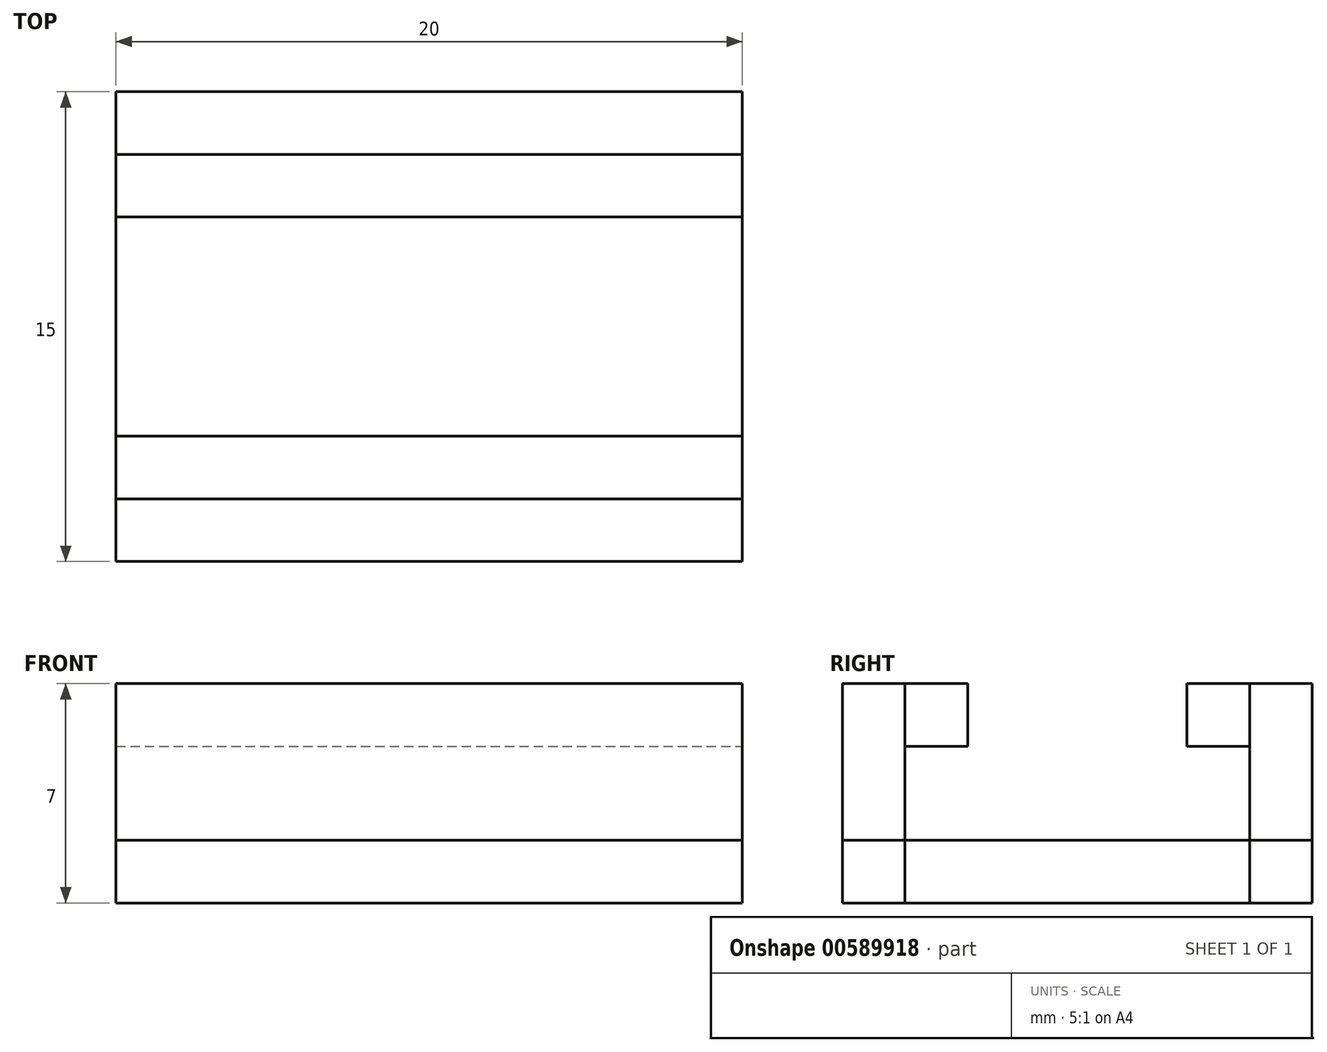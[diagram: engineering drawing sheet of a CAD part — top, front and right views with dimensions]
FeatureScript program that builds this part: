
annotation { "Feature Type Name" : "Feature", "Feature Type Description" : "" }
export const myFeature = defineFeature(function(context is Context, id is Id, definition is map)
    precondition{}
    {
        {
            var Q0;
            Q0=qCreatedBy(makeId("Top.planeOp"),FACE);
            var sketch = newSketch(context, id + "F0", { "sketchPlane" : qUnion([Q0])});
            skLineSegment(sketch, "E0.bottom", {"start": v(-43, 7.5) * mm, "end": v(-23, 7.5) * mm});
            skLineSegment(sketch, "E0.top", {"start": v(-43, -7.5) * mm, "end": v(-23, -7.5) * mm});
            skLineSegment(sketch, "E0.left", {"start": v(-43, 7.5) * mm, "end": v(-43, -7.5) * mm});
            skLineSegment(sketch, "E0.right", {"start": v(-23, 7.5) * mm, "end": v(-23, -7.5) * mm});
            skLineSegment(sketch, "E1.top", {"start": v(-43, 5.5) * mm, "end": v(-23, 5.5) * mm});
            skLineSegment(sketch, "E1.left", {"start": v(-43, 7.5) * mm, "end": v(-43, 5.5) * mm});
            skLineSegment(sketch, "E1.right", {"start": v(-23, 7.5) * mm, "end": v(-23, 5.5) * mm});
            skLineSegment(sketch, "E2.top", {"start": v(-43, 3.5) * mm, "end": v(-23, 3.5) * mm});
            skLineSegment(sketch, "E2.left", {"start": v(-43, 7.5) * mm, "end": v(-43, 3.5) * mm});
            skLineSegment(sketch, "E2.right", {"start": v(-23, 7.5) * mm, "end": v(-23, 3.5) * mm});
            skLineSegment(sketch, "E3.MirrorCS", {"start": v(-43, -3.5) * mm, "end": v(-23, -3.5) * mm});
            skLineSegment(sketch, "E4.MirrorCS", {"start": v(-43, -5.5) * mm, "end": v(-23, -5.5) * mm});
            skLineSegment(sketch, "E5.MirrorCS", {"start": v(-43, -7.5) * mm, "end": v(-43, -3.5) * mm});
            skLineSegment(sketch, "E6.MirrorCS", {"start": v(-23, -7.5) * mm, "end": v(-23, -3.5) * mm});
            skSolve(sketch);
        }
        {
            var Q0;
            {var subQ0=sQuery(id+"F0.wireOp",EDGE,"E0.top");Q0=makeQuery(id+"F0.imprint","IMPRINT",FACE,{"disambiguationData":[TD([[makeQuery(id+"F0.imprint","IMPRINT",EDGE,{"derivedFrom":subQ0}),1.0]])]});}
            var Q1;
            {var subQ0=sQuery(id+"F0.wireOp",EDGE,"E1.top");Q1=makeQuery(id+"F0.imprint","IMPRINT",FACE,{"disambiguationData":[TD([[makeQuery(id+"F0.imprint","IMPRINT",EDGE,{"derivedFrom":subQ0}),1.0]])]});}
            extrude(context, id + "F1", {"entities" : qUnion([Q0, Q1]), "depth" : 7 * mm, "offsetDistance" : 25 * mm});
        }
        {
            var Q0;
            Q0 = qSketchRegion(id + "F0", true);
            extrude(context, id + "F2", {"entities" : qUnion([Q0]), "depth" : 2 * mm, "offsetDistance" : 25 * mm});
        }
        {
            var Q0;
            {var subQ0=sQuery(id+"F0.wireOp",EDGE,"E1.top");Q0=makeQuery(id+"F0.imprint","IMPRINT",FACE,{"disambiguationData":[TD([[makeQuery(id+"F0.imprint","IMPRINT",EDGE,{"derivedFrom":subQ0}),-1.0]])]});}
            var Q1;
            {var subQ0=sQuery(id+"F0.wireOp",EDGE,"E3.MirrorCS");Q1=makeQuery(id+"F0.imprint","IMPRINT",FACE,{"disambiguationData":[TD([[makeQuery(id+"F0.imprint","IMPRINT",EDGE,{"derivedFrom":subQ0}),-1.0]])]});}
            extrude(context, id + "F3", {"entities" : qUnion([Q0, Q1]), "depth" : 7 * mm, "offsetDistance" : 25 * mm, "hasSecondDirection" : true, "secondDirectionOppositeDirection" : false, "secondDirectionDepth" : 5 * mm});
        }
    });
